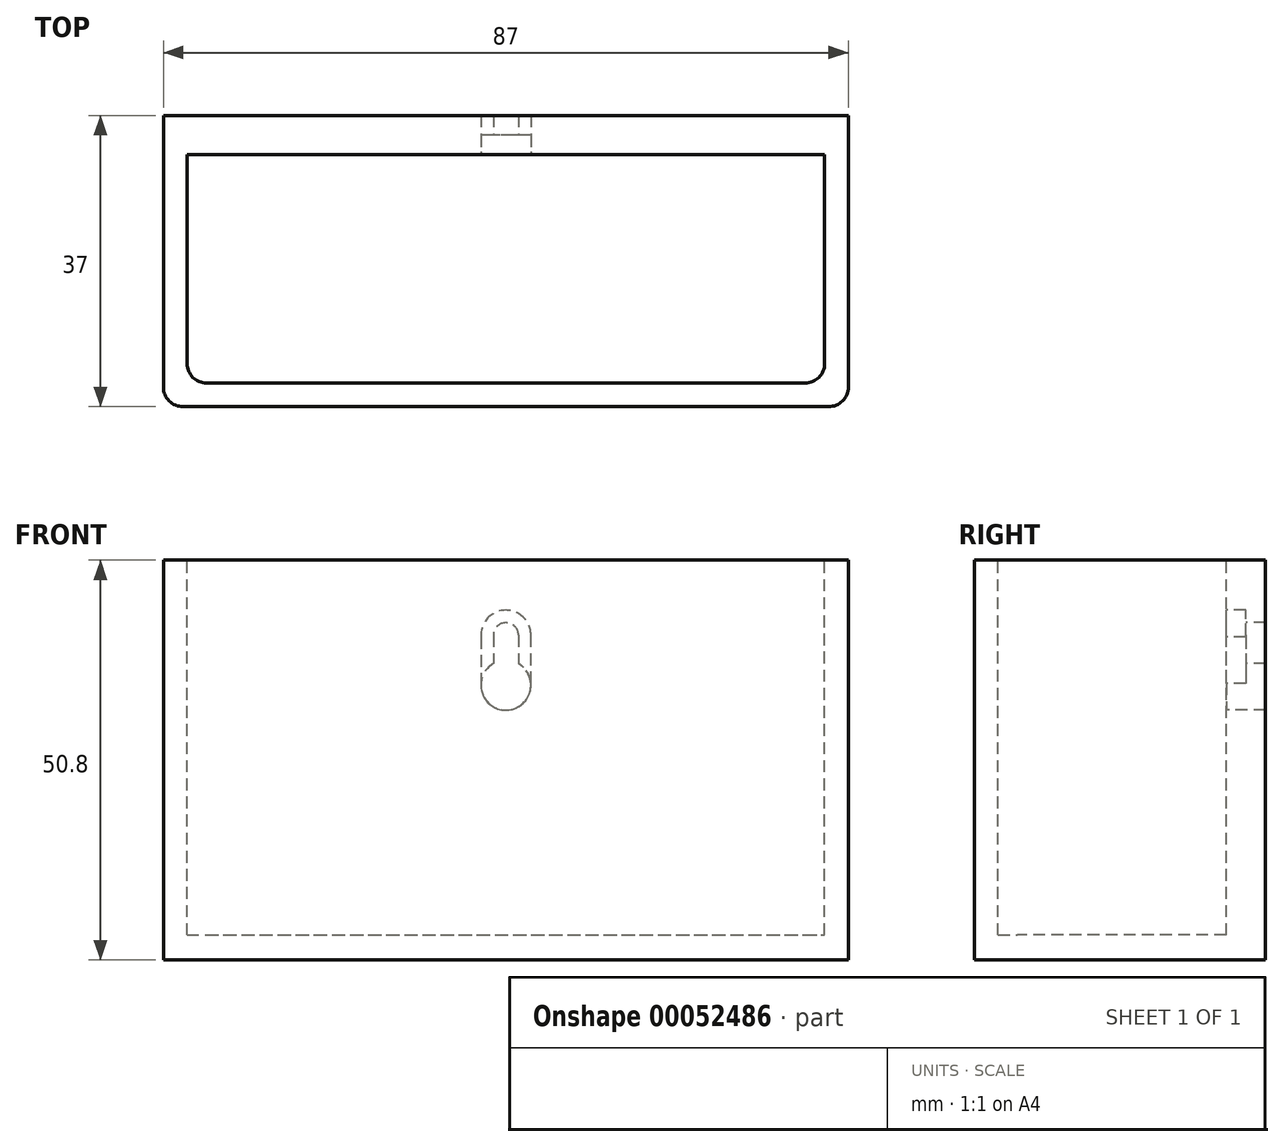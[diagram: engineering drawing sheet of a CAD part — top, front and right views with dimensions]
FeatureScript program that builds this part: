
annotation { "Feature Type Name" : "Feature", "Feature Type Description" : "" }
export const myFeature = defineFeature(function(context is Context, id is Id, definition is map)
    precondition{}
    {
        {
            var Q0;
            Q0=qCreatedBy(makeId("Top.planeOp"),FACE);
            var sketch = newSketch(context, id + "F0", { "sketchPlane" : qUnion([Q0])});
            skLineSegment(sketch, "E0.rect.bottom", {"start": v(43.5, -18.5) * mm, "end": v(-43.5, -18.5) * mm});
            skLineSegment(sketch, "E0.rect.top", {"start": v(43.5, 18.5) * mm, "end": v(-43.5, 18.5) * mm});
            skLineSegment(sketch, "E0.rect.left", {"start": v(43.5, -18.5) * mm, "end": v(43.5, 18.5) * mm});
            skLineSegment(sketch, "E0.rect.right", {"start": v(-43.5, -18.5) * mm, "end": v(-43.5, 18.5) * mm});
            skPoint(sketch, "E0.rect.middle", {"position": v(0, 0) * mm});
            skSolve(sketch);
        }
        {
            var Q0;
            Q0 = qSketchRegion(id + "F0", true);
            extrude(context, id + "F1", {"entities" : qUnion([Q0]), "depth" : 50.8 * mm});
        }
        {
            var Q0;
            Q0=makeQuery(id+"F1.opExtrude","CAP_FACE",FACE,{"disambiguationData":[OSD([sQuery(id+"F0.wireOp",EDGE,"E0.rect.bottom"),sQuery(id+"F0.wireOp",EDGE,"E0.rect.top"),sQuery(id+"F0.wireOp",EDGE,"E0.rect.left"),sQuery(id+"F0.wireOp",EDGE,"E0.rect.right")])],"isStart":false});
            var sketch = newSketch(context, id + "F2", { "sketchPlane" : qUnion([Q0])});
            skLineSegment(sketch, "E1.bottom", {"start": v(-40.5, 13.5) * mm, "end": v(40.5, 13.5) * mm});
            skLineSegment(sketch, "E1.top", {"start": v(-40.5, -15.5) * mm, "end": v(40.5, -15.5) * mm});
            skLineSegment(sketch, "E1.left", {"start": v(-40.5, 13.5) * mm, "end": v(-40.5, -15.5) * mm});
            skLineSegment(sketch, "E1.right", {"start": v(40.5, 13.5) * mm, "end": v(40.5, -15.5) * mm});
            skSolve(sketch);
        }
        {
            var Q0;
            Q0 = qSketchRegion(id + "F2", true);
            extrude(context, id + "F3", {"entities" : qUnion([Q0]), "operationType" : NewBodyOperationType.REMOVE, "oppositeDirection" : true, "depth" : 47.62 * mm});
        }
        {
            var Q0;
            Q0=makeQuery(id+"F1.opExtrude","SWEPT_EDGE",EDGE,{"disambiguationData":[OSD([sQuery(id+"F0.wireOp",EDGE,"E0.rect.bottom"),sQuery(id+"F0.wireOp",EDGE,"E0.rect.left")])]});
            var Q1;
            Q1=makeQuery(id+"F1.opExtrude","SWEPT_EDGE",EDGE,{"disambiguationData":[OSD([sQuery(id+"F0.wireOp",EDGE,"E0.rect.bottom"),sQuery(id+"F0.wireOp",EDGE,"E0.rect.right")])]});
            var Q2;
            Q2=makeQuery(id+"F3.boolean.opBoolean","COPY",EDGE,{"derivedFrom":makeQuery(id+"F3.opExtrude","SWEPT_EDGE",EDGE,{"disambiguationData":[OSD([sQuery(id+"F2.wireOp",EDGE,"E1.top"),sQuery(id+"F2.wireOp",EDGE,"E1.left")])]})});
            var Q3;
            Q3=makeQuery(id+"F3.boolean.opBoolean","COPY",EDGE,{"derivedFrom":makeQuery(id+"F3.opExtrude","SWEPT_EDGE",EDGE,{"disambiguationData":[OSD([sQuery(id+"F2.wireOp",EDGE,"E1.top"),sQuery(id+"F2.wireOp",EDGE,"E1.right")])]})});
            fillet(context, id + "F4", {"entities" : qUnion([Q0, Q1, Q2, Q3]), "radius" : 2.5 * mm, "tangentPropagation" : true, "allowEdgeOverflow" : false});
        }
        {
            var Q0;
            Q0=makeQuery(id+"F3.boolean.opBoolean","COPY",FACE,{"derivedFrom":makeQuery(id+"F3.opExtrude","SWEPT_FACE",FACE,{"disambiguationData":[OSD([sQuery(id+"F2.wireOp",EDGE,"E1.bottom")])]})});
            var sketch = newSketch(context, id + "F5", { "sketchPlane" : qUnion([Q0])});
            skArc(sketch, "E2", {"start": v(3.17, 41.05) * mm, "mid": v(0, 44.45) * mm, "end": v(-3.17, 41.05) * mm});
            skArc(sketch, "E3", {"start": v(-3.17, 35.15) * mm, "mid": v(0, 31.75) * mm, "end": v(3.17, 35.15) * mm});
            skLineSegment(sketch, "E4", {"start": v(-3.17, 41.5) * mm, "end": v(-3.17, 34.7) * mm});
            skLineSegment(sketch, "E5", {"start": v(3.17, 34.7) * mm, "end": v(3.17, 41.05) * mm});
            skSolve(sketch);
        }
        {
            var Q0;
            Q0 = qSketchRegion(id + "F5", true);
            extrude(context, id + "F6", {"entities" : qUnion([Q0]), "operationType" : NewBodyOperationType.REMOVE, "oppositeDirection" : true, "depth" : 2.5 * mm});
        }
        {
            var Q0;
            Q0=qCreatedBy(makeId("Front.planeOp"),FACE);
            var sketch = newSketch(context, id + "F7", { "sketchPlane" : qUnion([Q0])});
            skArc(sketch, "E6", {"start": v(-1.59, 37.67) * mm, "mid": v(0, 31.75) * mm, "end": v(1.59, 37.67) * mm});
            skArc(sketch, "E7", {"start": v(1.59, 41.28) * mm, "mid": v(0, 42.86) * mm, "end": v(-1.59, 41.28) * mm});
            skLineSegment(sketch, "E8", {"start": v(1.59, 41.28) * mm, "end": v(1.59, 37.67) * mm});
            skLineSegment(sketch, "E9", {"start": v(-1.59, 41.28) * mm, "end": v(-1.59, 37.67) * mm});
            skLineSegment(sketch, "E10", {"start": v(0, 41.28) * mm, "end": v(1.59, 41.28) * mm});
            skLineSegment(sketch, "E11", {"start": v(1.59, 41.28) * mm, "end": v(0, 41.28) * mm});
            skSolve(sketch);
        }
        {
            var Q0;
            Q0 = qSketchRegion(id + "F7", true);
            extrude(context, id + "F8", {"entities" : qUnion([Q0]), "operationType" : NewBodyOperationType.REMOVE, "oppositeDirection" : true, "depth" : 25.4 * mm});
        }
    });
